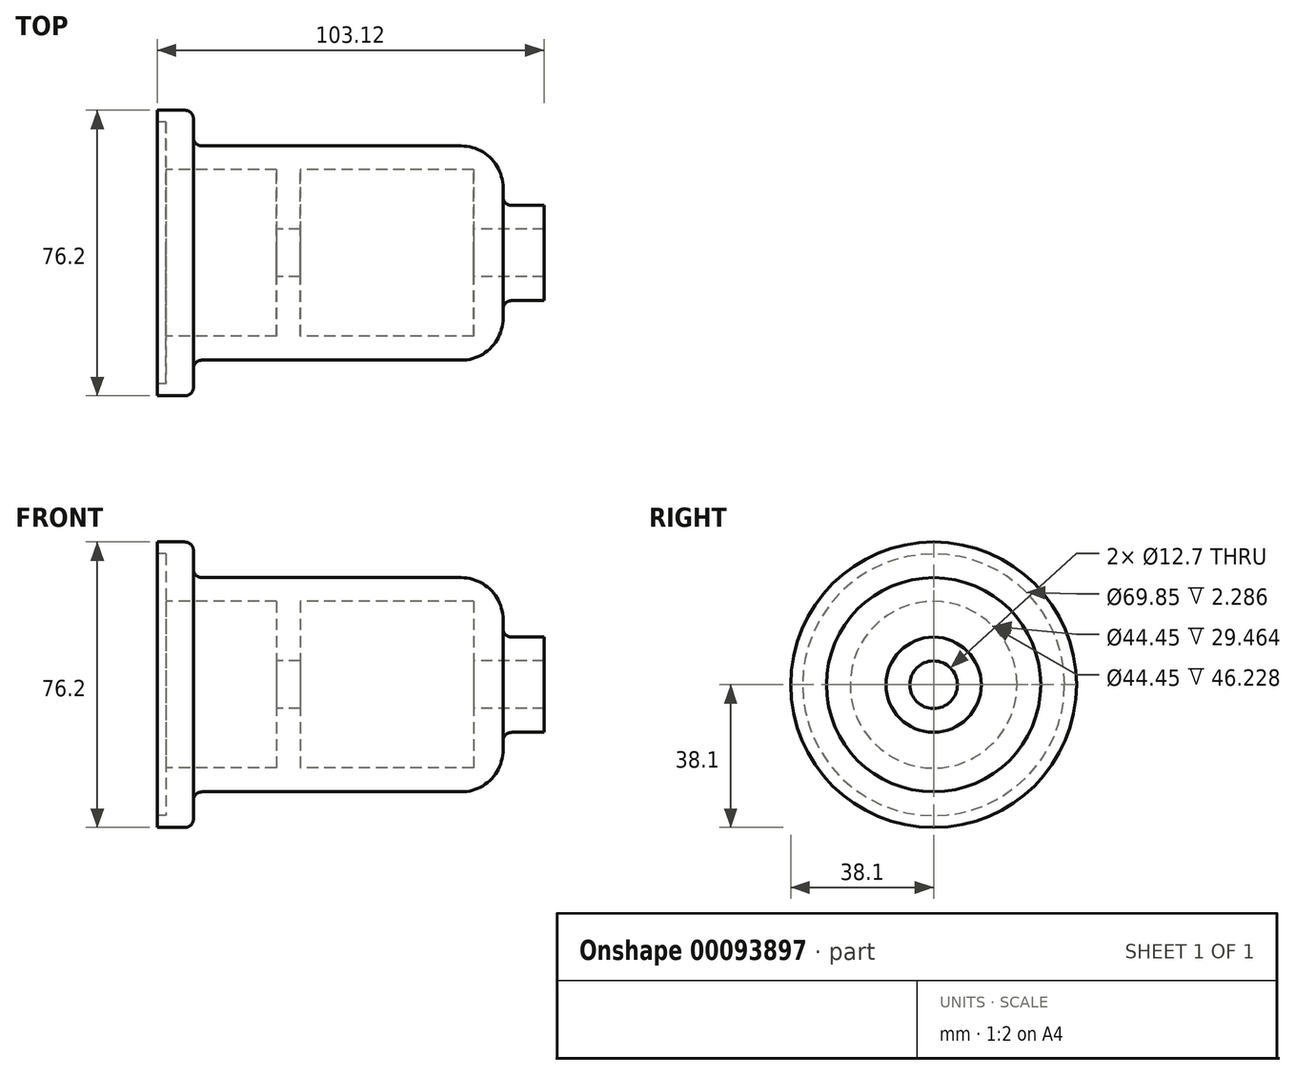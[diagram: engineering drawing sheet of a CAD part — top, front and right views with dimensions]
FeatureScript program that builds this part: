
annotation { "Feature Type Name" : "Feature", "Feature Type Description" : "" }
export const myFeature = defineFeature(function(context is Context, id is Id, definition is map)
    precondition{}
    {
        {
            var Q0;
            Q0=qCreatedBy(makeId("Front.planeOp"),FACE);
            var sketch = newSketch(context, id + "F0", { "sketchPlane" : qUnion([Q0])});
            skLineSegment(sketch, "E0", {"start": v(0, 0) * mm, "end": v(0, 12.7) * mm});
            skLineSegment(sketch, "E1", {"start": v(0, 12.7) * mm, "end": v(-8.64, 12.7) * mm});
            skLineSegment(sketch, "E2", {"start": v(-10.92, 14.99) * mm, "end": v(-10.92, 17.4) * mm});
            skLineSegment(sketch, "E3", {"start": v(-22.1, 28.58) * mm, "end": v(-91.19, 28.57) * mm});
            skLineSegment(sketch, "E4", {"start": v(-93.47, 30.86) * mm, "end": v(-93.47, 35.81) * mm});
            skLineSegment(sketch, "E5", {"start": v(-95.76, 38.1) * mm, "end": v(-103.12, 38.1) * mm});
            skLineSegment(sketch, "E6", {"start": v(-103.12, 38.1) * mm, "end": v(-103.12, 0) * mm});
            skLineSegment(sketch, "E7", {"start": v(-103.12, 0) * mm, "end": v(0, 0) * mm});
            skLineSegment(sketch, "E8", {"start": v(-103.12, 34.92) * mm, "end": v(-100.84, 34.92) * mm});
            skLineSegment(sketch, "E9", {"start": v(-100.84, 34.92) * mm, "end": v(-100.84, 22.22) * mm});
            skLineSegment(sketch, "E10", {"start": v(-100.84, 22.22) * mm, "end": v(-71.37, 22.22) * mm});
            skLineSegment(sketch, "E11", {"start": v(-71.37, 22.22) * mm, "end": v(-71.37, 6.35) * mm});
            skLineSegment(sketch, "E12", {"start": v(-71.37, 6.35) * mm, "end": v(-65.02, 6.35) * mm});
            skLineSegment(sketch, "E13", {"start": v(-65.02, 6.35) * mm, "end": v(-65.02, 22.22) * mm});
            skLineSegment(sketch, "E14", {"start": v(-65.02, 22.22) * mm, "end": v(-18.8, 22.22) * mm});
            skLineSegment(sketch, "E15", {"start": v(-18.8, 22.22) * mm, "end": v(-18.8, 6.35) * mm});
            skLineSegment(sketch, "E16", {"start": v(-18.8, 6.35) * mm, "end": v(0, 6.35) * mm});
            skArc(sketch, "E17", {"start": v(-10.92, 17.4) * mm, "mid": v(-14.2, 25.3) * mm, "end": v(-22.1, 28.58) * mm});
            skArc(sketch, "E18", {"start": v(-10.92, 14.99) * mm, "mid": v(-10.25, 13.37) * mm, "end": v(-8.64, 12.7) * mm});
            skArc(sketch, "E19", {"start": v(-93.47, 30.86) * mm, "mid": v(-92.8, 29.24) * mm, "end": v(-91.19, 28.57) * mm});
            skArc(sketch, "E20", {"start": v(-93.47, 35.81) * mm, "mid": v(-94.14, 37.43) * mm, "end": v(-95.76, 38.1) * mm});
            skSolve(sketch);
        }
        {
            var Q0;
            {var subQ4=sQuery(id+"F0.wireOp",EDGE,"E1");Q0=makeQuery(id+"F0.imprint","IMPRINT",FACE,{"disambiguationData":[TD([[makeQuery(id+"F0.imprint","IMPRINT",EDGE,{"derivedFrom":subQ4}),1.0]])]});}
            var Q1;
            Q1=sQuery(id+"F0.wireOp",EDGE,"E7");
            revolve(context, id + "F1", {"entities" : qUnion([Q0]), "axis" : qUnion([Q1]), "revolveType" : RevolveType.FULL});
        }
    });
